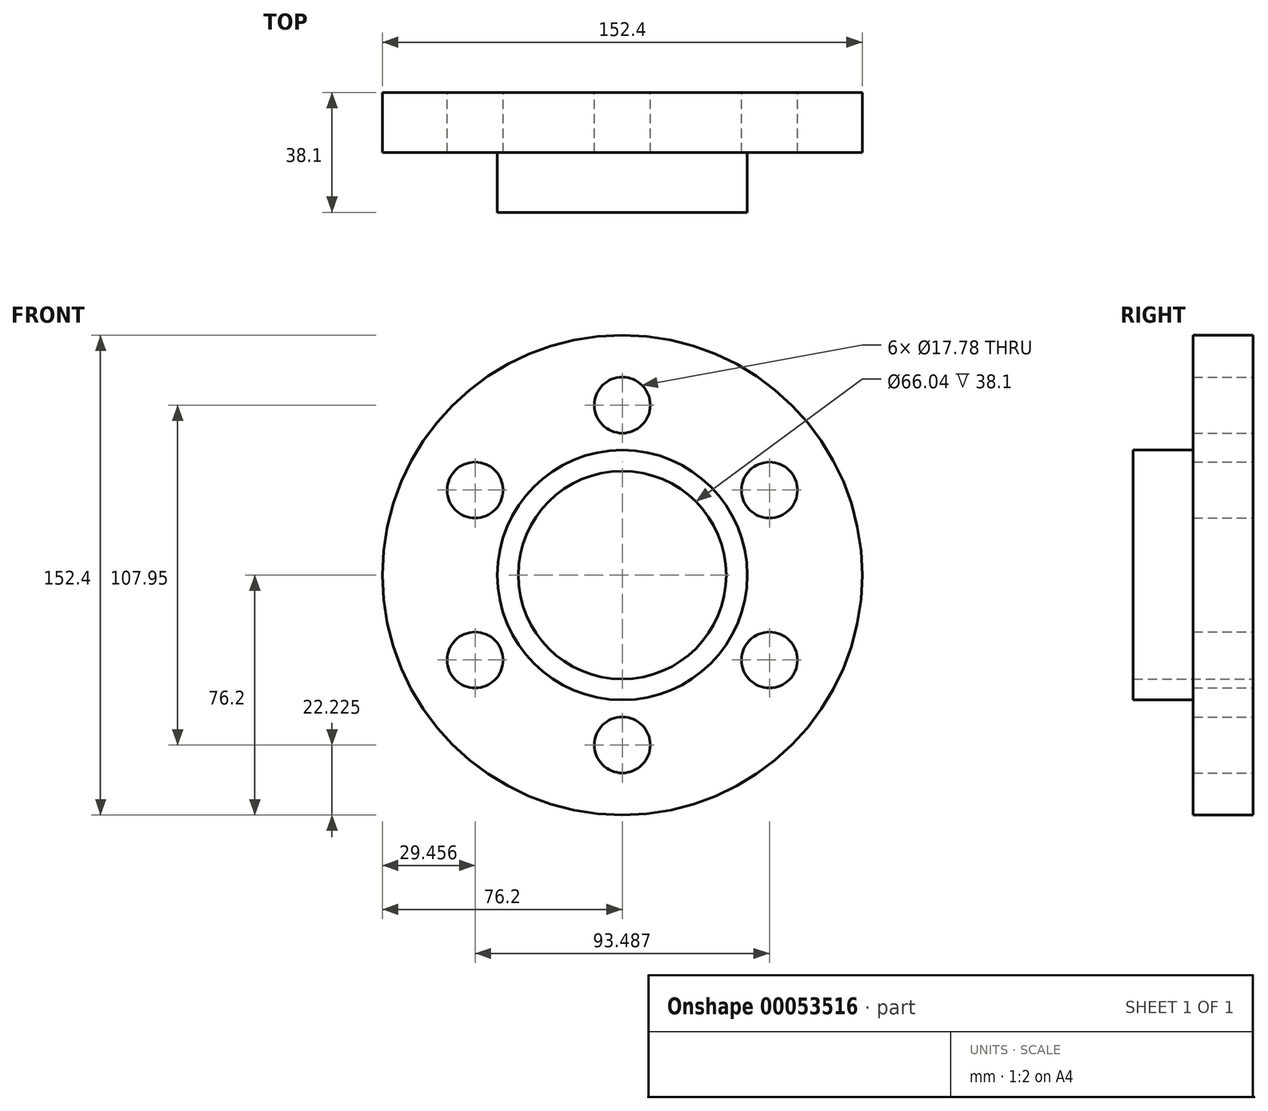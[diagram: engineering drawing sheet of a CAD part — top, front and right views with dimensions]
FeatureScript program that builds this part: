
annotation { "Feature Type Name" : "Feature", "Feature Type Description" : "" }
export const myFeature = defineFeature(function(context is Context, id is Id, definition is map)
    precondition{}
    {
        {
            var Q0;
            Q0=qCreatedBy(makeId("Front.planeOp"),FACE);
            var sketch = newSketch(context, id + "F0", { "sketchPlane" : qUnion([Q0])});
            skCircle(sketch, "E0", {"center": v(0, 0) * mm, "radius": 76.2 * mm});
            skCircle(sketch, "E1", {"center": v(0, 53.98) * mm, "radius": 8.9 * mm});
            skPoint(sketch, "E2.center", {"position": v(0, 0.95) * mm});
            skCircle(sketch, "E3.1.0", {"center": v(-46.74, 26.99) * mm, "radius": 8.9 * mm});
            skCircle(sketch, "E3.2.0", {"center": v(-46.74, -26.99) * mm, "radius": 8.9 * mm});
            skCircle(sketch, "E3.3.0", {"center": v(0, -53.98) * mm, "radius": 8.9 * mm});
            skCircle(sketch, "E3.4.0", {"center": v(46.74, -26.99) * mm, "radius": 8.9 * mm});
            skCircle(sketch, "E3.5.0", {"center": v(46.74, 26.99) * mm, "radius": 8.9 * mm});
            skSolve(sketch);
        }
        {
            var Q0;
            Q0=makeQuery(id+"F0.imprint","IMPRINT",FACE,{"disambiguationData":[TD([[makeQuery(id+"F0.imprint","IMPRINT",EDGE,{"derivedFrom":sQuery(id+"F0.wireOp",EDGE,"E0")}),1.0]])]});
            extrude(context, id + "F1", {"entities" : qUnion([Q0]), "depth" : 19.05 * mm});
        }
        {
            var Q0;
            Q0=makeQuery(id+"F1.opExtrude","CAP_FACE",FACE,{"disambiguationData":[OSD([sQuery(id+"F0.wireOp",EDGE,"E0"),sQuery(id+"F0.wireOp",EDGE,"E1"),sQuery(id+"F0.wireOp",EDGE,"E2.1.0"),sQuery(id+"F0.wireOp",EDGE,"E2.2.0"),sQuery(id+"F0.wireOp",EDGE,"E2.3.0"),sQuery(id+"F0.wireOp",EDGE,"E2.4.0"),sQuery(id+"F0.wireOp",EDGE,"E2.5.0")])],"isStart":false});
            var sketch = newSketch(context, id + "F2", { "sketchPlane" : qUnion([Q0])});
            skCircle(sketch, "E4", {"center": v(0, 0) * mm, "radius": 39.69 * mm});
            skCircle(sketch, "E5", {"center": v(0, 0) * mm, "radius": 33.02 * mm});
            skSolve(sketch);
        }
        {
            var Q0;
            Q0=makeQuery(id+"F2.imprint","IMPRINT",FACE,{"disambiguationData":[TD([[makeQuery(id+"F2.imprint","IMPRINT",EDGE,{"derivedFrom":sQuery(id+"F2.wireOp",EDGE,"E4")}),1.0]])]});
            extrude(context, id + "F3", {"entities" : qUnion([Q0]), "operationType" : NewBodyOperationType.ADD, "depth" : 19.05 * mm});
        }
        {
            var Q0;
            Q0=makeQuery(id+"F3.boolean.opBoolean","SPLIT",FACE,{"disambiguationData":[TD([makeQuery(id+"F3.opExtrude","SWEPT_FACE",FACE,{"disambiguationData":[OSD([sQuery(id+"F2.wireOp",EDGE,"E5")])]})])],"derivedFrom":makeQuery(id+"F1.opExtrude","CAP_FACE",FACE,{"disambiguationData":[OSD([sQuery(id+"F0.wireOp",EDGE,"E0"),sQuery(id+"F0.wireOp",EDGE,"E1"),sQuery(id+"F0.wireOp",EDGE,"E2.1.0"),sQuery(id+"F0.wireOp",EDGE,"E2.2.0"),sQuery(id+"F0.wireOp",EDGE,"E2.3.0"),sQuery(id+"F0.wireOp",EDGE,"E2.4.0"),sQuery(id+"F0.wireOp",EDGE,"E2.5.0")])],"isStart":false})});
            var sketch = newSketch(context, id + "F4", { "sketchPlane" : qUnion([Q0])});
            skCircle(sketch, "E6", {"center": v(0, 0) * mm, "radius": 33.02 * mm});
            skSolve(sketch);
        }
        {
            var Q0;
            Q0=makeQuery(id+"F4.imprint","IMPRINT",FACE,{"disambiguationData":[TD([[makeQuery(id+"F4.imprint","IMPRINT",EDGE,{"derivedFrom":sQuery(id+"F4.wireOp",EDGE,"E6")}),1.0]])]});
            extrude(context, id + "F5", {"entities" : qUnion([Q0]), "operationType" : NewBodyOperationType.REMOVE, "oppositeDirection" : true, "depth" : 25.4 * mm});
        }
    });
